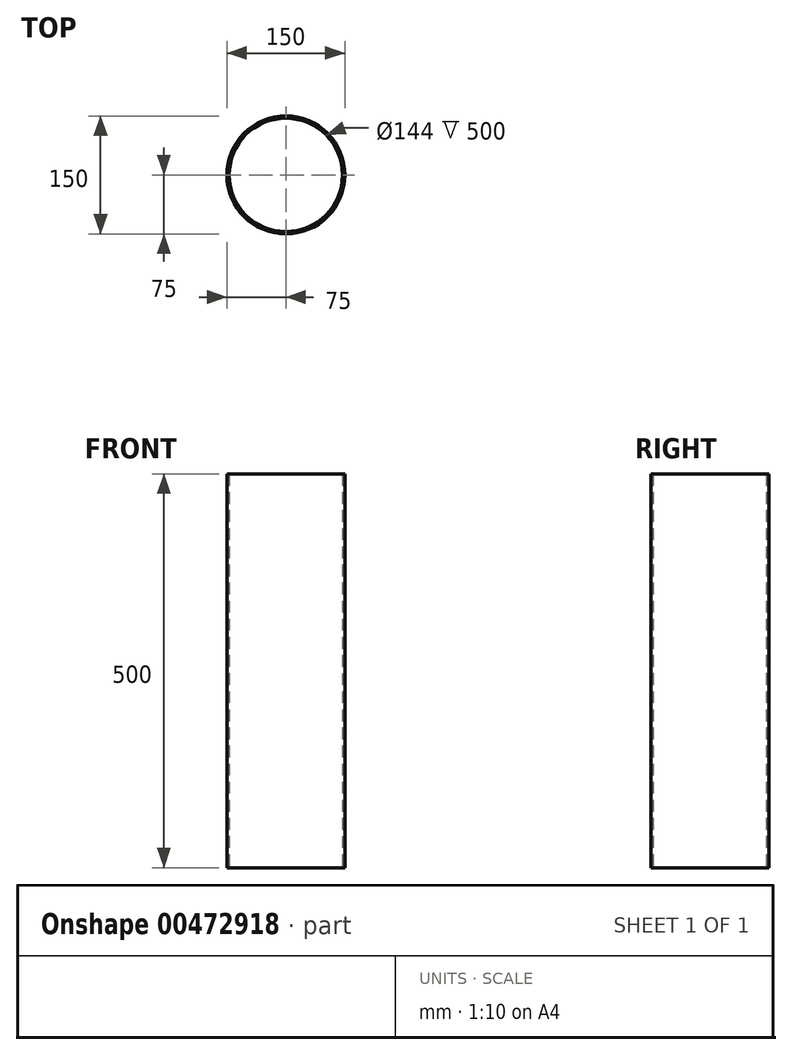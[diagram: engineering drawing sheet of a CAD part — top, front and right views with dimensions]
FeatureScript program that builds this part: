
annotation { "Feature Type Name" : "Feature", "Feature Type Description" : "" }
export const myFeature = defineFeature(function(context is Context, id is Id, definition is map)
    precondition{}
    {
        {
            var Q0;
            Q0=qCreatedBy(makeId("Top.planeOp"),FACE);
            var sketch = newSketch(context, id + "F0", { "sketchPlane" : qUnion([Q0])});
            skCircle(sketch, "E0", {"center": v(0, 0) * mm, "radius": 75 * mm});
            skCircle(sketch, "E1.0", {"center": v(0, 0) * mm, "radius": 72 * mm});
            skSolve(sketch);
        }
        {
            var Q0;
            Q0=qSketchRegion(id+"F0",true);
            extrude(context, id + "F1", {"entities" : qUnion([Q0]), "depth" : 500 * mm});
        }
    });
